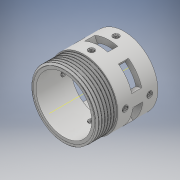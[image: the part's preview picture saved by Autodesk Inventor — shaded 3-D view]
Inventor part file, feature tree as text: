
AUTODESK INVENTOR PART (.ipt)
format: ipt  version: 2018 (Build 220112000, 112)  size: 4,931,584 bytes
history: native  units: mm
features: sketch x23, revolve x12, thread x9, helix x9, other x5, plane x3, extrude x1, hole x1, pattern_circular x1
ambient origin geometry x8: Origin, YZ Plane, XZ Plane, XY Plane, X Axis, Y Axis, Z Axis, Center Point
bodies: Solid1 (feature_tree), Solid2 (feature_tree), Solid12 (feature_tree), Solid13 (feature_tree), Solid14 (feature_tree), Solid15 (feature_tree), Solid16 (feature_tree), Solid17 (feature_tree), Solid18 (feature_tree), Solid19 (feature_tree)
feature tree (64):
  revolve  "Revolution1"  [1 undecoded]
  thread  "Thread1"  [1 undecoded]
  revolve  "Revolution2"  [1 undecoded]
  revolve  "Revolution3"  Angle=90.0deg
  helix  "Coil1"  [1 undecoded]
  plane  "Work Plane1"
  extrude  "Extrusion1"  Depth=3.0mm
  plane  "Work Plane3"
  revolve  "Revolution4"  [1 undecoded]
  other  "Work Axis1"
  other  "Work Axis2"
  plane  "Work Plane5"
  hole  "Hole2"  [1 undecoded]
  pattern_circular  "Circular Pattern2"  Count=6 Angle=360.0deg
  thread  "Thread11"  [1 undecoded]
  thread  "Thread12"  [1 undecoded]
  thread  "Thread13"  [1 undecoded]
  thread  "Thread14"  [1 undecoded]
  thread  "Thread15"  [1 undecoded]
  thread  "Thread16"  [1 undecoded]
  thread  "Thread17"  [1 undecoded]
  thread  "Thread18"  [1 undecoded]
  revolve  "Revolution14"  [1 undecoded]
  helix  "Coil11"  [1 undecoded]
  revolve  "Revolution15"  [1 undecoded]
  helix  "Coil12"  [1 undecoded]
  revolve  "Revolution16"  [1 undecoded]
  helix  "Coil13"  [1 undecoded]
  revolve  "Revolution17"  [1 undecoded]
  helix  "Coil14"  [1 undecoded]
  revolve  "Revolution18"  [1 undecoded]
  helix  "Coil15"  [1 undecoded]
  revolve  "Revolution19"  [1 undecoded]
  helix  "Coil16"  [1 undecoded]
  revolve  "Revolution20"  [1 undecoded]
  helix  "Coil17"  [1 undecoded]
  revolve  "Revolution21"  [1 undecoded]
  helix  "Coil18"  [1 undecoded]
  sketch  "Sketch1"  dims[d0=5.0mm d1=20.0mm d2=70.0mm]
  sketch  "Sketch2"  dims[d3=27.75mm d4=6.0mm]
  sketch  "Sketch3"  dims[d5=15.0mm d6=90.0deg d7=10.0mm d8=0.0mm]
  sketch  "Sketch4"  dims[d9=9.599311mm d10=0.480249mm d11=0.480249mm d14=3.0mm]
  sketch  "Sketch5"  dims[d16=9.599311mm d18=0.0mm]
  sketch  "Sketch7"  dims[d19=0.0mm]
  sketch  "Sketch9"  dims[d20=3.003mm d21=26.0mm d22=10.0mm d23=0.0mm d24=0.0mm d25=0.0mm d26=0.0mm d27=0.0mm d28=29.75mm d33=60.0mm d35=360.0deg d37=10.0mm d38=0.0mm d40=0.0mm d41=15.0mm d42=6.0mm d43=90.0deg]
  other  "Work Axis3"
  other  "Work Axis4"
  other  "Work Axis5"
  sketch  "Sketch28"  dims[d51=6.0mm d52=6.0mm d53=4.0mm d54=2.0mm d55=90.0deg d56=8.0mm d57=20.594885mm d86=9.599311mm d104=9.599311mm d122=9.599311mm]
  sketch  "Sketch29"  dims[d140=9.599311mm d158=9.599311mm d176=9.599311mm]
  sketch  "Sketch30"  dims[d194=9.599311mm d212=9.599311mm d230=9.599311mm]
  sketch  "Sketch31"  dims[d241=40.0mm d242=360.0deg d244=10.0mm d245=0.0mm d246=10.0mm d247=0.0mm]
  sketch  "Sketch32"  dims[d248=10.0mm d249=0.0mm d250=10.0mm d251=0.0mm d252=10.0mm d253=0.0mm]
  sketch  "Sketch33"  dims[d254=10.0mm d255=0.0mm d256=10.0mm d257=0.0mm d258=10.0mm d259=0.0mm]
  sketch  "Sketch34"  dims[d260=9.599311mm d261=0.160083mm d262=0.160083mm d265=1.0mm d267=9.599311mm]
  sketch  "Sketch35"  dims[d269=0.0mm]
  sketch  "Sketch36"  dims[d270=1.001mm d271=8.162639mm d272=10.0mm d273=0.0mm d274=0.0mm d275=0.0mm d276=0.0mm d277=0.0mm d278=9.599311mm d279=0.160083mm d280=0.160083mm d283=1.0mm]
  sketch  "Sketch37"  dims[d285=9.599311mm d287=0.0mm]
  sketch  "Sketch38"  dims[d288=1.001mm d289=8.162639mm d290=10.0mm d291=0.0mm d292=0.0mm d293=0.0mm d294=0.0mm d295=0.0mm d296=9.599311mm d297=0.160083mm d298=0.160083mm]
  sketch  "Sketch39"  dims[d301=1.0mm]
  sketch  "Sketch40"  dims[d303=9.599311mm]
  sketch  "Sketch41"  dims[d305=0.0mm]
  sketch  "Sketch42"  dims[d306=1.001mm d307=8.162639mm d308=10.0mm d309=0.0mm d310=0.0mm d311=0.0mm d312=0.0mm d313=0.0mm]
  sketch  "Sketch43"  dims[d314=9.599311mm d315=0.160083mm d316=0.160083mm d319=1.0mm d321=9.599311mm d323=0.0mm d324=1.001mm d325=8.162639mm d326=10.0mm d327=0.0mm d328=0.0mm d329=0.0mm d330=0.0mm d331=0.0mm d332=9.599311mm d333=0.160083mm d334=0.160083mm d337=1.0mm d339=9.599311mm d341=0.0mm d342=1.001mm d343=8.162639mm d344=10.0mm d345=0.0mm d346=0.0mm d347=0.0mm d348=0.0mm d349=0.0mm d350=9.599311mm d351=0.160083mm d352=0.160083mm d355=1.0mm d357=9.599311mm d359=0.0mm d360=1.001mm d361=8.162639mm d362=10.0mm d363=0.0mm d364=0.0mm d365=0.0mm d366=0.0mm d367=0.0mm d368=9.599311mm d369=0.160083mm d370=0.160083mm d373=1.0mm d375=9.599311mm d377=0.0mm d378=1.001mm d379=8.162639mm d380=10.0mm d381=0.0mm d382=0.0mm d383=0.0mm d384=0.0mm d385=0.0mm d386=9.599311mm d387=0.160083mm d388=0.160083mm d391=1.0mm d393=9.599311mm d395=0.0mm d396=1.001mm d397=8.162639mm d398=10.0mm d399=0.0mm d400=0.0mm d401=0.0mm d402=0.0mm d403=0.0mm d44=1.0mm d45=1.0mm]
note: 30 required parameter values undecoded (feature->parameter linkage not recoverable at this tier; creation-order binding heuristic only, values carry confidence <= 0.55)